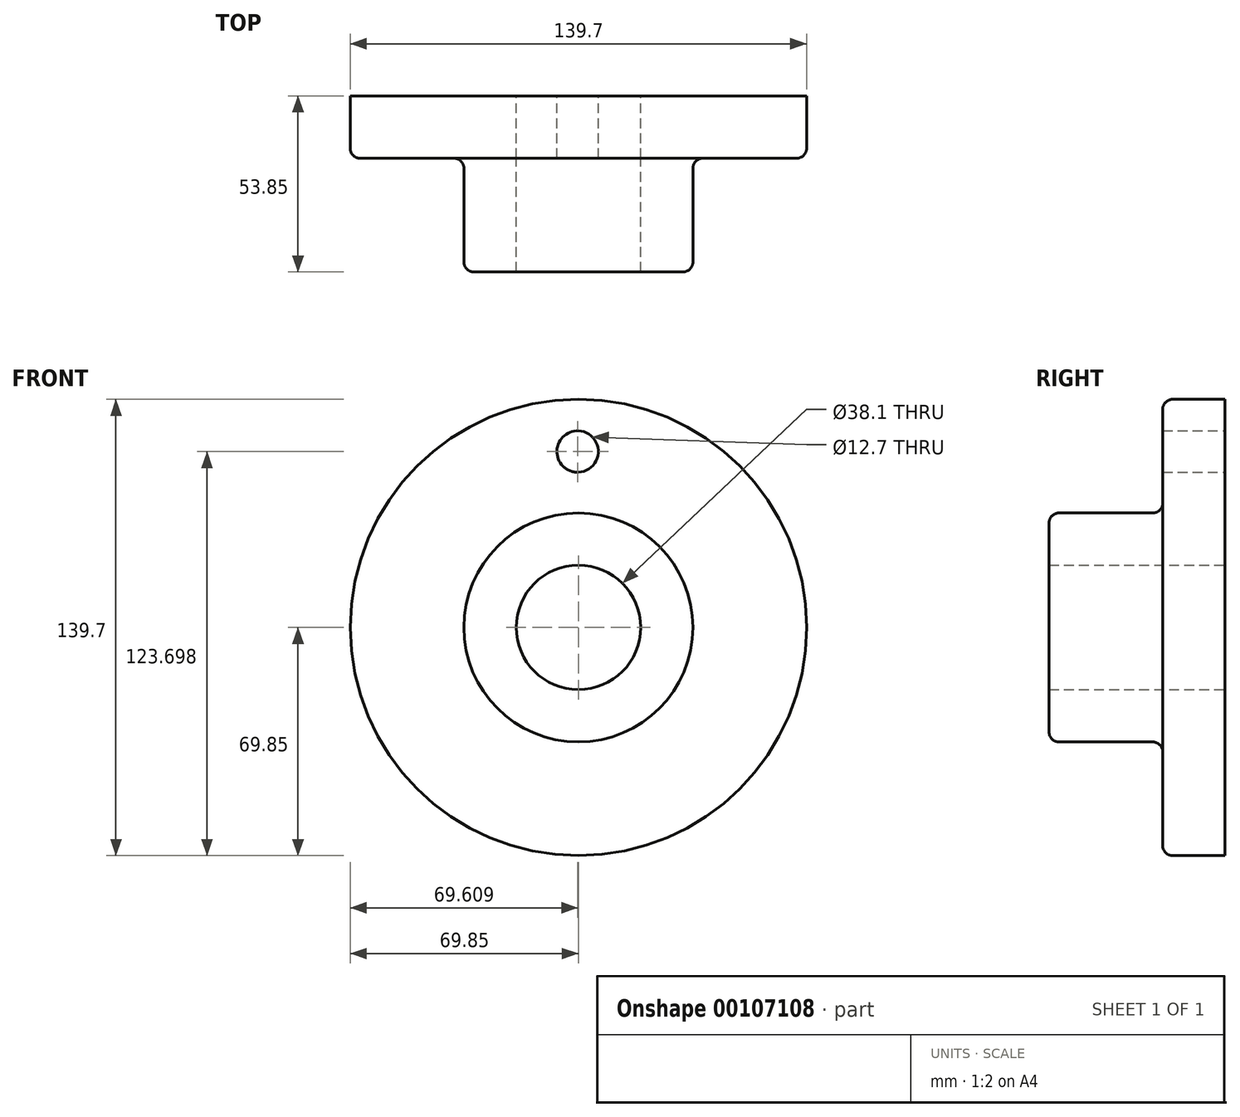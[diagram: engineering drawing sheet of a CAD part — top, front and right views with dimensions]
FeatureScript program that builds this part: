
annotation { "Feature Type Name" : "Feature", "Feature Type Description" : "" }
export const myFeature = defineFeature(function(context is Context, id is Id, definition is map)
    precondition{}
    {
        {
            var Q0;
            Q0=qCreatedBy(makeId("Top.planeOp"),FACE);
            var sketch = newSketch(context, id + "F0", { "sketchPlane" : qUnion([Q0])});
            skLineSegment(sketch, "E0", {"start": v(0, 0) * mm, "end": v(50.8, 0) * mm});
            skLineSegment(sketch, "E1", {"start": v(0, -53.85) * mm, "end": v(0, 0) * mm});
            skPoint(sketch, "E2.visualSharp", {"position": v(50.8, -19.05) * mm});
            skPoint(sketch, "E3.visualSharp", {"position": v(16, -53.85) * mm});
            skLineSegment(sketch, "E4", {"start": v(-19.05, 0) * mm, "end": v(-19.05, -54.63) * mm, "construction": true});
            skLineSegment(sketch, "E5", {"start": v(-54.1, -56.12) * mm, "end": v(-54.1, 4.6) * mm, "construction": true});
            skLineSegment(sketch, "E6", {"start": v(-38.1, -55.72) * mm, "end": v(-38.1, 5.54) * mm, "construction": true});
            skLineSegment(sketch, "E7", {"start": v(16, -53.85) * mm, "end": v(16, -19.05) * mm});
            skLineSegment(sketch, "E8", {"start": v(0, -53.85) * mm, "end": v(16, -53.85) * mm});
            skLineSegment(sketch, "E9", {"start": v(15.78, -19.05) * mm, "end": v(50.8, -19.05) * mm});
            skLineSegment(sketch, "E10", {"start": v(50.8, -19.05) * mm, "end": v(50.8, 0) * mm});
            skSolve(sketch);
        }
        {
            var Q0;
            Q0=makeQuery(id+"F0.imprint","IMPRINT",FACE,{"disambiguationData":[TD([[makeQuery(id+"F0.imprint","IMPRINT",EDGE,{"derivedFrom":sQuery(id+"F0.wireOp",EDGE,"E0")}),-1.0]])]});
            var Q1;
            Q1=sQuery(id+"F0.wireOp",EDGE,"E4");
            revolve(context, id + "F1", {"entities" : qUnion([Q0]), "axis" : qUnion([Q1]), "revolveType" : RevolveType.FULL});
        }
        {
            var Q0;
            Q0=makeQuery(id+"F1.opRevolve","SWEPT_EDGE",EDGE,{"disambiguationData":[OSD([sQuery(id+"F0.wireOp",EDGE,"E9"),sQuery(id+"F0.wireOp",EDGE,"E10")])]});
            var Q1;
            Q1=makeQuery(id+"F1.opRevolve","SWEPT_EDGE",EDGE,{"disambiguationData":[OSD([sQuery(id+"F0.wireOp",EDGE,"E7"),sQuery(id+"F0.wireOp",EDGE,"E9")])]});
            var Q2;
            Q2=makeQuery(id+"F1.opRevolve","SWEPT_EDGE",EDGE,{"disambiguationData":[OSD([sQuery(id+"F0.wireOp",EDGE,"E7"),sQuery(id+"F0.wireOp",EDGE,"E8")])]});
            fillet(context, id + "F2", {"entities" : qUnion([Q0, Q1, Q2]), "radius" : 3.05 * mm, "tangentPropagation" : true, "allowEdgeOverflow" : false});
        }
        {
            var Q0;
            Q0=qCreatedBy(makeId("Front.planeOp"),FACE);
            var sketch = newSketch(context, id + "F3", { "sketchPlane" : qUnion([Q0])});
            skCircle(sketch, "E11", {"center": v(-19.3, 53.85) * mm, "radius": 6.35 * mm});
            skCircle(sketch, "E12", {"center": v(-19.3, 0) * mm, "radius": 53.85 * mm, "construction": true});
            skSolve(sketch);
        }
        {
            var Q0;
            Q0=makeQuery(id+"F3.imprint","IMPRINT",FACE,{"disambiguationData":[TD([[makeQuery(id+"F3.imprint","IMPRINT",EDGE,{"derivedFrom":sQuery(id+"F3.wireOp",EDGE,"E11")}),1.0]])]});
            extrude(context, id + "F4", {"entities" : qUnion([Q0]), "operationType" : NewBodyOperationType.REMOVE, "endBound" : BoundingType.THROUGH_ALL, "depth" : 25.4 * mm});
        }
    });
